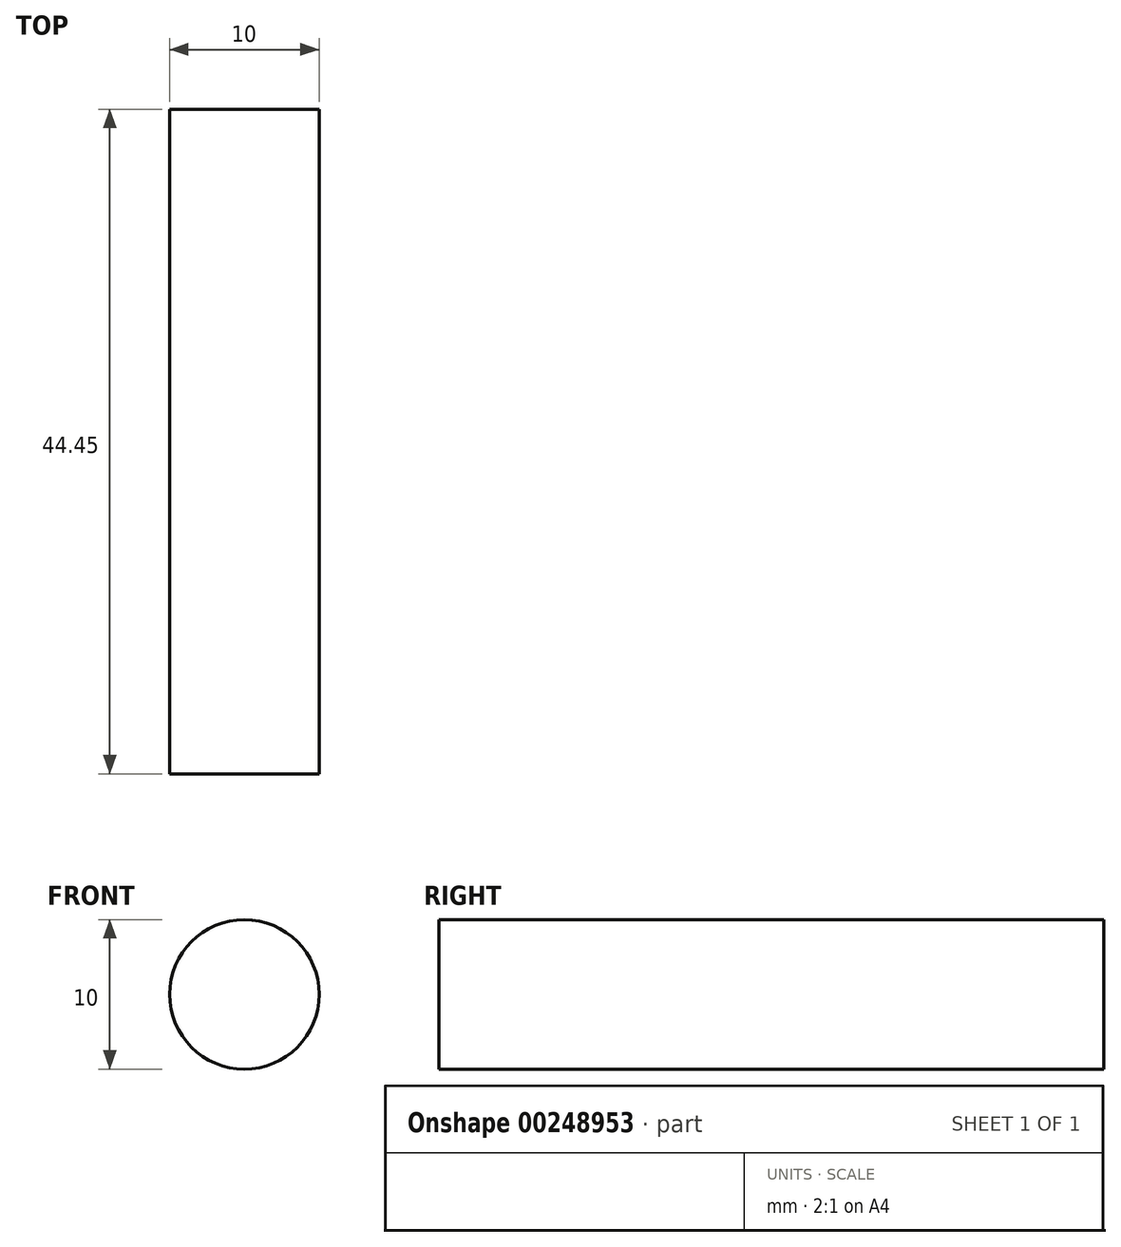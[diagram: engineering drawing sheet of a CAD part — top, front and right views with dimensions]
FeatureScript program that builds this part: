
annotation { "Feature Type Name" : "Feature", "Feature Type Description" : "" }
export const myFeature = defineFeature(function(context is Context, id is Id, definition is map)
    precondition{}
    {
        {
            var Q0;
            Q0=qCreatedBy(makeId("Front.planeOp"),FACE);
            var sketch = newSketch(context, id + "F0", { "sketchPlane" : qUnion([Q0])});
            skCircle(sketch, "E0", {"center": v(18.68, 12.5) * mm, "radius": 5 * mm});
            skSolve(sketch);
        }
        {
            var Q0;
            Q0=makeQuery(id+"F0.imprint","IMPRINT",FACE,{"disambiguationData":[TD([[makeQuery(id+"F0.imprint","IMPRINT",EDGE,{"derivedFrom":sQuery(id+"F0.wireOp",EDGE,"E0")}),1.0]])]});
            extrude(context, id + "F1", {"entities" : qUnion([Q0]), "depth" : 44.45 * mm});
        }
    });
